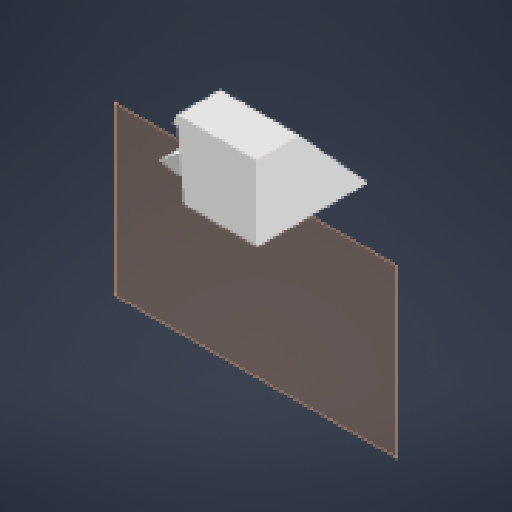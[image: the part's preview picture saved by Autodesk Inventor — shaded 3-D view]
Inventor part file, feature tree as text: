
AUTODESK INVENTOR PART (.ipt)
format: ipt  version: 2024 (Build 280153000, 153)  size: 149,504 bytes
history: native  units: in
note: dims shown in document units (in); Inventor stores cm internally (conversion verified against a paired STEP export)
features: reference x6, chamfer x4, extrude x3, sketch x3, other x3, plane x1
ambient origin geometry x8: Origin, YZ Plane, XZ Plane, XY Plane, X Axis, Y Axis, Z Axis, Center Point
bodies: Solid1 (feature_tree)
feature tree (20):
  plane  "Work Plane1"
  extrude  "Extrusion1"  Depth=1.15in
  extrude  "Extrusion2"  Depth=0.1575in
  chamfer  "Chamfer1"  Distance=3.0965in
  chamfer  "Chamfer2"  Distance=1.8025in
  chamfer  "Chamfer3"  Distance=1.125in
  chamfer  "Chamfer4"  Distance=1.125in
  extrude  "Extrusion3"  Depth=0.5906in TaperAngle=15.0deg
  sketch  "Sketch1"  dims[d0=1.15in d1=0.8933in]
  reference  "Reference1"
  sketch  "Sketch2"  dims[d2=0.1575in d3=0.1575in d4=3.0965in d5=0.0in d6=1.8025in d7=0.0in d8=1.125in d9=0.125in d10=0.2749in d11=1.125in d12=0.125in d13=0.2749in]
  reference  "Reference2"
  sketch  "Sketch3"  dims[d14=0.3125in d15=0.125in d16=15.0deg d17=0.3125in d18=0.125in d19=15.0deg d20=0.5906in d21=0.0in]
  reference  "Reference3"
  reference  "Reference4"
  reference  "Reference5"
  reference  "Reference6"
  other  "<userpath>\Desktop\SeniorDesign\Head_V3\Head_V3_Assembly.iam"
  other  "Head_V3_Assembly.iam"
  other  "Head_Top:1"
